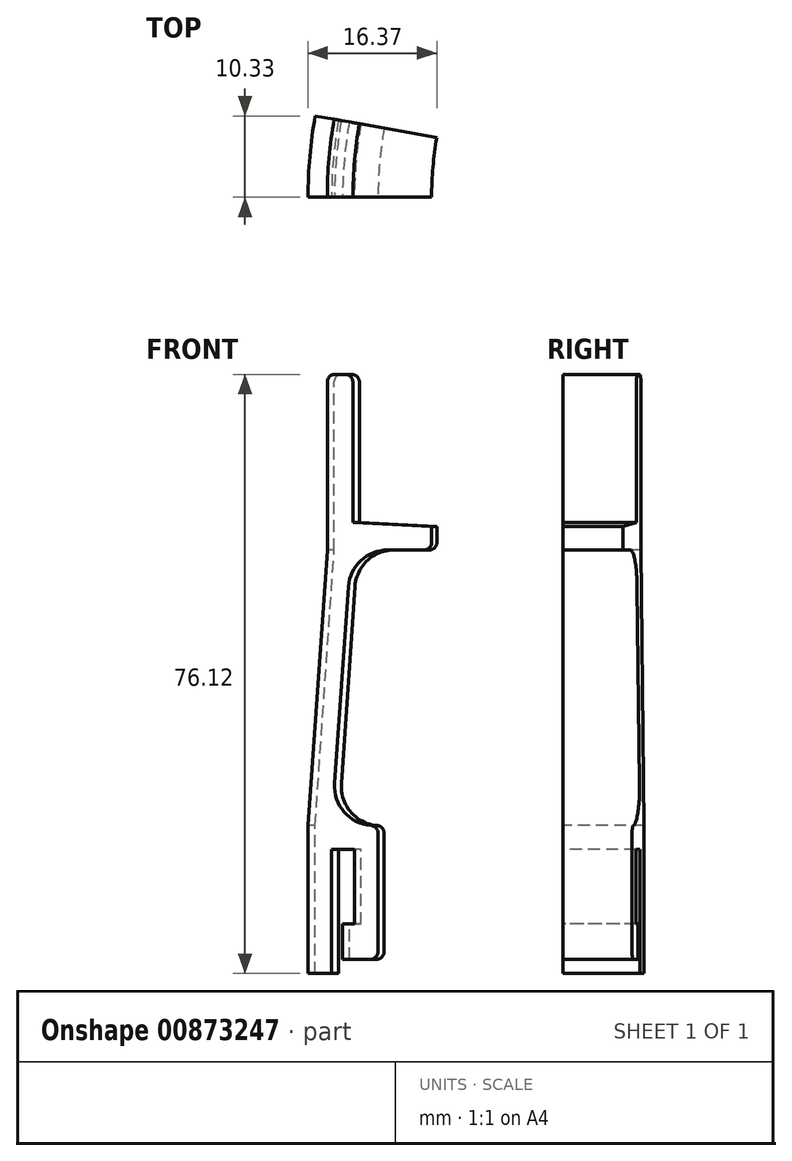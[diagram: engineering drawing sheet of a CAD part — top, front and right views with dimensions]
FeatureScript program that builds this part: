
annotation { "Feature Type Name" : "Feature", "Feature Type Description" : "" }
export const myFeature = defineFeature(function(context is Context, id is Id, definition is map)
    precondition{}
    {
        {
            var Q0;
            Q0=qCreatedBy(makeId("Front.planeOp"),FACE);
            var sketch = newSketch(context, id + "F0", { "sketchPlane" : qUnion([Q0])});
            skLineSegment(sketch, "E0", {"start": v(0, 0) * mm, "end": v(-3, 0) * mm});
            skLineSegment(sketch, "E1", {"start": v(-3, 0) * mm, "end": v(-3, 18.8) * mm});
            skLineSegment(sketch, "E2", {"start": v(-3, 18.8) * mm, "end": v(5.9, 18.8) * mm});
            skLineSegment(sketch, "E3", {"start": v(5.9, 18.8) * mm, "end": v(5.9, 1.8) * mm});
            skLineSegment(sketch, "E4", {"start": v(5.9, 1.8) * mm, "end": v(1.4, 1.8) * mm});
            skLineSegment(sketch, "E5", {"start": v(1.4, 1.8) * mm, "end": v(1.4, 6.3) * mm});
            skLineSegment(sketch, "E6", {"start": v(1.4, 6.3) * mm, "end": v(2.9, 6.3) * mm});
            skLineSegment(sketch, "E7", {"start": v(2.9, 6.3) * mm, "end": v(2.9, 15.8) * mm});
            skLineSegment(sketch, "E8", {"start": v(2.9, 15.8) * mm, "end": v(0, 15.8) * mm});
            skLineSegment(sketch, "E9", {"start": v(0, 15.8) * mm, "end": v(0, 0) * mm});
            skLineSegment(sketch, "E10", {"start": v(12.7, 56.8) * mm, "end": v(12.7, 53.8) * mm});
            skLineSegment(sketch, "E11", {"start": v(12.7, 53.8) * mm, "end": v(-0.55, 53.8) * mm});
            skPoint(sketch, "E12.endSnap0", {"position": v(1.45, 18.8) * mm});
            skLineSegment(sketch, "E13", {"start": v(56.5, 69.3) * mm, "end": v(56.5, -16.8) * mm, "construction": true});
            skLineSegment(sketch, "E14", {"start": v(0, 18.8) * mm, "end": v(2.45, 53.8) * mm});
            skLineSegment(sketch, "E15", {"start": v(-3, 18.8) * mm, "end": v(-0.55, 53.8) * mm});
            skLineSegment(sketch, "E16", {"start": v(2.45, 53.8) * mm, "end": v(2.7, 57.32) * mm, "construction": true});
            skLineSegment(sketch, "E17", {"start": v(2.7, 57.32) * mm, "end": v(2.7, 76.12) * mm});
            skLineSegment(sketch, "E18", {"start": v(2.7, 76.12) * mm, "end": v(-0.55, 76.12) * mm});
            skLineSegment(sketch, "E19", {"start": v(-0.55, 53.8) * mm, "end": v(-0.55, 76.12) * mm});
            skLineSegment(sketch, "E20.trimOffspring", {"start": v(2.7, 57.32) * mm, "end": v(12.7, 56.8) * mm});
            skSolve(sketch);
        }
        {
            var Q0;
            {var subQ0=sQuery(id+"F0.wireOp",EDGE,"EBBtCbmr-cya3-o5bh-EbWE-XZrQBtWqaYjX");Q0=makeQuery(id+"F0.imprint","IMPRINT",FACE,{"disambiguationData":[TD([[makeQuery(id+"F0.imprint","IMPRINT",EDGE,{"derivedFrom":subQ0}),-1.0]])]});}
            var Q1;
            Q1=makeQuery(id+"F0.imprint","IMPRINT",FACE,{"disambiguationData":[TD([[makeQuery(id+"F0.imprint","IMPRINT",EDGE,{"derivedFrom":sQuery(id+"F0.wireOp",EDGE,"E0")}),-1.0]])]});
            var Q2;
            {var subQ2=sQuery(id+"F0.wireOp",EDGE,"E14");Q2=makeQuery(id+"F0.imprint","IMPRINT",FACE,{"disambiguationData":[TD([[makeQuery(id+"F0.imprint","IMPRINT",EDGE,{"derivedFrom":subQ2}),1.0]])]});}
            var Q3;
            {var subQ4=sQuery(id+"F0.wireOp",EDGE,"E10");Q3=makeQuery(id+"F0.imprint","IMPRINT",FACE,{"disambiguationData":[TD([[makeQuery(id+"F0.imprint","IMPRINT",EDGE,{"derivedFrom":subQ4}),-1.0]])]});}
            var Q4;
            Q4=sQuery(id+"F0.wireOp",EDGE,"E13");
            revolve(context, id + "F1", {"surfaceOperationType" : NewSurfaceOperationType.NEW, "entities" : qUnion([Q0, Q1, Q2, Q3]), "axis" : qUnion([Q4]), "revolveType" : RevolveType.ONE_DIRECTION, "angle" : 10 * degree});
        }
        {
            var Q0;
            Q0=makeQuery(id+"F1.opRevolve","SWEPT_EDGE",EDGE,{"disambiguationData":[OSD([sQuery(id+"F0.wireOp",EDGE,"E2"),sQuery(id+"F0.wireOp",EDGE,"E14")])]});
            var Q1;
            Q1=makeQuery(id+"F1.opRevolve","SWEPT_EDGE",EDGE,{"disambiguationData":[OSD([sQuery(id+"F0.wireOp",EDGE,"E11"),sQuery(id+"F0.wireOp",EDGE,"E14")])]});
            fillet(context, id + "F2", {"entities" : qUnion([Q0, Q1]), "radius" : 5 * mm, "tangentPropagation" : true, "allowEdgeOverflow" : false});
        }
        {
            var Q0;
            Q0=makeQuery(id+"F1.opRevolve","SWEPT_EDGE",EDGE,{"disambiguationData":[OSD([sQuery(id+"F0.wireOp",EDGE,"E3"),sQuery(id+"F0.wireOp",EDGE,"E4")])]});
            var Q1;
            Q1=makeQuery(id+"F1.opRevolve","SWEPT_EDGE",EDGE,{"disambiguationData":[OSD([sQuery(id+"F0.wireOp",EDGE,"E2"),sQuery(id+"F0.wireOp",EDGE,"E3")])]});
            var Q2;
            Q2=makeQuery(id+"F1.opRevolve","SWEPT_EDGE",EDGE,{"disambiguationData":[OSD([sQuery(id+"F0.wireOp",EDGE,"RSjyuGSd-hVhm-sjjQ-vVsk-fJQsQTp197Ck"),sQuery(id+"F0.wireOp",EDGE,"RMuFD9mW-NZSk-sQMc-vdIR-NBgBKlThQNfU")])]});
            var Q3;
            Q3=makeQuery(id+"F1.opRevolve","SWEPT_EDGE",EDGE,{"disambiguationData":[OSD([sQuery(id+"F0.wireOp",EDGE,"EBBtCbmr-cya3-o5bh-EbWE-XZrQBtWqaYjX"),sQuery(id+"F0.wireOp",EDGE,"RSjyuGSd-hVhm-sjjQ-vVsk-fJQsQTp197Ck")])]});
            var Q4;
            Q4=makeQuery(id+"F1.opRevolve","SWEPT_EDGE",EDGE,{"disambiguationData":[OSD([sQuery(id+"F0.wireOp",EDGE,"E10"),sQuery(id+"F0.wireOp",EDGE,"E11")])]});
            var Q5;
            Q5=makeQuery(id+"F1.opRevolve","SWEPT_EDGE",EDGE,{"disambiguationData":[OSD([sQuery(id+"F0.wireOp",EDGE,"E17"),sQuery(id+"F0.wireOp",EDGE,"E18")])]});
            var Q6;
            Q6=makeQuery(id+"F1.opRevolve","SWEPT_EDGE",EDGE,{"disambiguationData":[OSD([sQuery(id+"F0.wireOp",EDGE,"E18"),sQuery(id+"F0.wireOp",EDGE,"E19")])]});
            fillet(context, id + "F3", {"entities" : qUnion([Q0, Q1, Q2, Q3, Q4, Q5, Q6]), "radius" : 1 * mm, "tangentPropagation" : true, "allowEdgeOverflow" : false});
        }
    });
